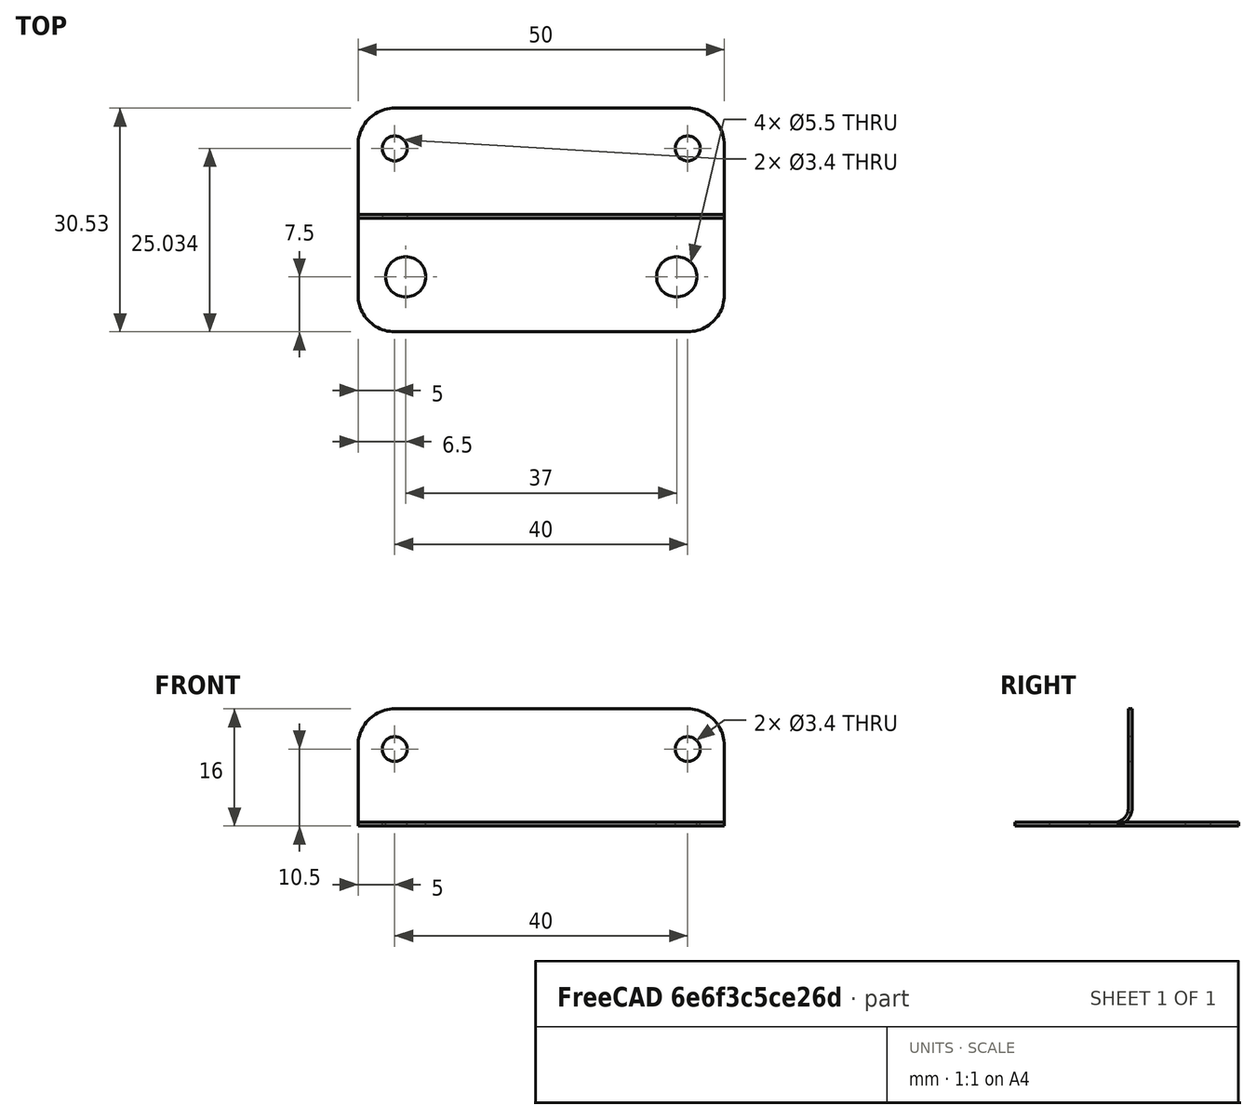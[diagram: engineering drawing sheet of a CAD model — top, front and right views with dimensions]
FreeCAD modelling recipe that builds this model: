
FCSTD DOCUMENT  (FreeCAD 1.1R38827 (Git))
Label: ugol90degX40mm
License: All rights reserved
LicenseURL: http://en.wikipedia.org/wiki/All_rights_reserved
objects: TechDraw::DrawViewDimension×10, Sketcher::SketchObject×8, PartDesign::SubShapeBinder×3, TechDraw::DrawViewPart×3, PartDesign::Hole×2, PartDesign::FeaturePython×1, TechDraw::DrawSVGTemplate×1, PartDesign::CoordinateSystem×1, PartDesign::Fillet×1, PartDesign::Mirrored×1, PartDesign::Body×1, Part::Feature×1, TechDraw::DrawPage×1
note: 38 computed .brp shape members not serialized (recipe doc carries the construction recipe); baked Part::Feature solids carry a one-line shape summary decoded from their .brp

FEATURE [Sketcher::SketchObject] Sketch
  ArcFitTolerance = 0
  AttachmentSupport = -> [YZ_Plane]
  FullyConstrained = true
  MakeInternals = false
  MapMode = 5
  Placement = pos=(0,0,0) rot=(0.57735,0.57735,0.57735;2.0944rad)
  sketch-geometry (2):
    g0: LineSegment StartX=-16 StartY=0 StartZ=0 EndX=0 EndY=0 EndZ=0
    g1: LineSegment StartX=0 StartY=0 StartZ=0 EndX=0 EndY=16 EndZ=0
  constraints (6):
    c: PointOnObject(g0,g-1)
    c: Coincident(g0,g-1)
    c: Coincident(g0,g1)
    c: PointOnObject(g1,g-2)
    c: DistanceX(g0,g0) = 16  'length'
    c: DistanceY(g1,g1) = 16  'height'
FEATURE [PartDesign::FeaturePython] BaseBend  # WARN: FeaturePython — macro-defined, semantics opaque (R4)
  BendSide = 1
  BendSketch = -> Sketch
  MidPlane = true
  Reverse = false
  Suppressed = false
  length = 50
  radius = 2
  thickness = 0.5
FEATURE [Sketcher::SketchObject] Sketch001
  ArcFitTolerance = 0
  AttachmentOffset = pos=(0,-8.5,0) rot=(0,0,1;0rad)
  AttachmentSupport = -> [XY_Plane]
  FullyConstrained = true
  MakeInternals = false
  MapMode = 5
  Placement = pos=(0,-8.5,0) rot=(0,0,1;0rad)
  sketch-geometry (2):
    g0: Circle CenterX=18.5 CenterY=0 CenterZ=0 NormalX=0 NormalY=0 NormalZ=1 AngleXU=0 Radius=1.7
    g1: Circle CenterX=-18.5 CenterY=0 CenterZ=0 NormalX=0 NormalY=0 NormalZ=1 AngleXU=0 Radius=1.7
  constraints (5):
    c: PointOnObject(g0,g-1)
    c: Equal(g1,g0)
    c: Diameter(g1) = 3.4
    c: Symmetric(g0,g1,g-2)
    c: DistanceX(g1,g0) = 37
FEATURE [PartDesign::SubShapeBinder] Binder  label="hor"
  BindCopyOnChange = 0
  BindMode = 0
  ClaimChildren = true
  Context = -> Body [Binder.]
  Fuse = false
  MakeFace = true
  OffsetFill = false
  OffsetIntersection = false
  OffsetJoinType = 0
  OffsetOpenResult = false
  PartialLoad = false
  Relative = true
  Support = -> [Sketch001]
  _Version = 2
FEATURE [PartDesign::SubShapeBinder] Binder001
  BindCopyOnChange = 0
  BindMode = 0
  ClaimChildren = false
  Context = -> Body [Binder001.]
  Fuse = false
  MakeFace = true
  OffsetFill = false
  OffsetIntersection = false
  OffsetJoinType = 0
  OffsetOpenResult = false
  PartialLoad = false
  Placement = pos=(0,0,0) rot=(-1,0,0;1.5708rad)
  Relative = true
  Support = -> [Sketch001]
  _Version = 2
FEATURE [PartDesign::SubShapeBinder] Binder002  label="vert"
  BindCopyOnChange = 0
  BindMode = 0
  ClaimChildren = true
  Context = -> Body [Binder002.]
  Fuse = false
  MakeFace = true
  OffsetFill = false
  OffsetIntersection = false
  OffsetJoinType = 0
  OffsetOpenResult = false
  PartialLoad = false
  Relative = true
  Support = -> [Sketch003]
  _Version = 2
  expr: Support = Sketch003._self
FEATURE [PartDesign::Hole] Hole
  BaseFeature = -> BaseBend
  CustomThreadClearance = 0
  Depth = 25
  DepthType = 0
  Diameter = 5.5
  DrillForDepth = false
  DrillPoint = 1
  DrillPointAngle = 118
  HoleCutCountersinkAngle = 90
  HoleCutCustomValues = false
  HoleCutDepth = 0
  HoleCutDiameter = 6.1
  HoleCutType = 0
  ModelThread = false
  Profile = -> Binder
  Reversed = true
  Suppressed = false
  Tapered = false
  TaperedAngle = 90
  ThreadClass = 0
  ThreadDepth = 25
  ThreadDepthType = 0
  ThreadDirection = 0
  ThreadFit = 0
  ThreadSize = 0
  ThreadType = 0
  Threaded = false
  UseCustomThreadClearance = false
FEATURE [PartDesign::Hole] Hole001
  BaseFeature = -> Hole
  CustomThreadClearance = 0
  Depth = 25
  DepthType = 0
  Diameter = 3.4
  DrillForDepth = false
  DrillPoint = 1
  DrillPointAngle = 118
  HoleCutCountersinkAngle = 90
  HoleCutCustomValues = false
  HoleCutDepth = 0
  HoleCutDiameter = 6.1
  HoleCutType = 0
  ModelThread = false
  Profile = -> Binder002
  Suppressed = false
  Tapered = false
  TaperedAngle = 90
  ThreadClass = 0
  ThreadDepth = 25
  ThreadDepthType = 0
  ThreadDirection = 0
  ThreadFit = 0
  ThreadSize = 0
  ThreadType = 0
  Threaded = false
  UseCustomThreadClearance = false
FEATURE [Sketcher::SketchObject] Sketch002
  ArcFitTolerance = 0
  AttachmentOffset = pos=(25,-16,0) rot=(0,0,1;-1.5708rad)
  AttachmentSupport = -> [XY_Plane]
  FullyConstrained = true
  MakeInternals = false
  MapMode = 5
  Placement = pos=(25,-16,0) rot=(0,0,1;4.71239rad)
  expr: .AttachmentOffset.Base.x = BaseBend.length / 2
  expr: .AttachmentOffset.Base.y = -Sketch.Constraints.length
  sketch-geometry (3):
    g0: ArcOfCircle CenterX=-5 CenterY=-5 CenterZ=0 NormalX=0 NormalY=0 NormalZ=1 AngleXU=0 Radius=5 StartAngle=0 EndAngle=1.5708
    g1: LineSegment StartX=-1.6e-14 StartY=-5 StartZ=0 EndX=-1.6e-14 EndY=-1.6e-14 EndZ=0
    g2: LineSegment StartX=-1.6e-14 StartY=-1.6e-14 StartZ=0 EndX=-5 EndY=-1.6e-14 EndZ=0
  constraints (8):
    c: PointOnObject(g0,g-1)
    c: PointOnObject(g0,g-2)
    c: Coincident(g1,g2)
    c: Horizontal(g2)
    c: Vertical(g1)
    c: Tangent(g0,g1) = -1.5708
    c: Tangent(g2,g0) = -1.5708
    c: Diameter(g0) = 10
FEATURE [TechDraw::DrawSVGTemplate] Template
  Height = 210
  Orientation = 1
  Template = <path>
  Width = 297
FEATURE [PartDesign::CoordinateSystem] Local_CS
  AttacherType = Attacher::AttachEngine3D
  AttachmentSupport = -> [XY_Plane]
  MapMode = 5
FEATURE [Sketcher::SketchObject] Sketch003
  ArcFitTolerance = 0
  AttachmentSupport = -> [XZ_Plane]
  FullyConstrained = true
  MakeInternals = false
  MapMode = 5
  Placement = pos=(0,0,0) rot=(1,0,0;1.5708rad)
  expr: Constraints[3] = 3.4
  sketch-geometry (2):
    g0: Circle CenterX=20 CenterY=10.5 CenterZ=0 NormalX=0 NormalY=0 NormalZ=1 AngleXU=0 Radius=1.7
    g1: Circle CenterX=-20 CenterY=10.5 CenterZ=0 NormalX=0 NormalY=0 NormalZ=1 AngleXU=0 Radius=1.7
  constraints (5):
    c: Symmetric(g1,g0,g-2)
    c: DistanceX(g1,g0) = 40
    c: Equal(g0,g1)
    c: Diameter(g0) = 3.4
    c: DistanceY(g0) = 10.5
FEATURE [PartDesign::Fillet] Fillet
  Base = -> Hole001 [Edge33,Edge15]
  BaseFeature = -> Hole001
  Radius = 5
  SupportTransform = false
  Suppressed = false
  UseAllEdges = false
FEATURE [PartDesign::Mirrored] Mirrored
  BaseFeature = -> Fillet
  MirrorPlane = -> YZ_Plane
  Originals = -> [Fillet]
  Suppressed = false
  TransformMode = 0
FEATURE [PartDesign::Body] Body  label="Body_material_0.50ansi"
  AllowCompound = false
  Group = -> [Sketch,BaseBend,Sketch001,Binder,Binder001,Binder002,Hole,Hole001,Sketch002,Local_CS,Sketch003,Fillet,Mirrored]
  Origin = -> Origin
  Tip = -> Mirrored
FEATURE [TechDraw::DrawViewPart] View
  CoarseView = false
  Direction = (1,0,0)
  Focus = 100
  HardHidden = false
  IsoCount = 0
  IsoHidden = false
  IsoVisible = false
  LockPosition = false
  Perspective = false
  Rotation = 0
  ScaleType = 0
  ScrubCount = 0
  SeamHidden = false
  SeamVisible = true
  SmoothHidden = false
  SmoothVisible = true
  Source = -> [Body]
  X = 234.919
  XDirection = (0,1,-1.19209e-07)
  Y = 105
  expr: Y = Template.Height / 2
FEATURE [TechDraw::DrawViewPart] View001
  CoarseView = false
  Direction = (0,-1,0)
  Focus = 100
  HardHidden = false
  IsoCount = 0
  IsoHidden = false
  IsoVisible = false
  LockPosition = false
  Perspective = false
  Rotation = 0
  ScaleType = 0
  ScrubCount = 0
  SeamHidden = false
  SeamVisible = true
  SmoothHidden = false
  SmoothVisible = true
  Source = -> [Body]
  X = 150.495
  XDirection = (1,0,0)
  Y = 105
  expr: Y = Template.Height / 2
FEATURE [TechDraw::DrawViewDimension] Dimension004
  AngleOverride = false
  Arbitrary = false
  ArbitraryTolerances = false
  EqualTolerance = true
  ExtensionAngle = 0
  FormatSpec = %.2w
  FormatSpecOverTolerance = %+.2w
  FormatSpecUnderTolerance = %+.2w
  Inverted = false
  LineAngle = 0
  LockPosition = false
  MeasureType = 1
  OverTolerance = 0
  References2D = -> [View001]
  Rotation = 0
  ScaleType = 0
  TheoreticalExact = false
  Type = 1
  UnderTolerance = 0
  X = -2.33735
  Y = 6.64929
FEATURE [TechDraw::DrawViewDimension] Dimension005
  AngleOverride = false
  Arbitrary = false
  ArbitraryTolerances = false
  EqualTolerance = true
  ExtensionAngle = 0
  FormatSpec = %.2w
  FormatSpecOverTolerance = %+.2w
  FormatSpecUnderTolerance = %+.2w
  Inverted = false
  LineAngle = 0
  LockPosition = false
  MeasureType = 1
  OverTolerance = 0
  References2D = -> [View]
  Rotation = 0
  ScaleType = 0
  TheoreticalExact = false
  Type = 1
  UnderTolerance = 0
  X = -0.501878
  Y = -11.8128
FEATURE [TechDraw::DrawViewDimension] Dimension006
  AngleOverride = false
  Arbitrary = false
  ArbitraryTolerances = false
  EqualTolerance = true
  ExtensionAngle = 0
  FormatSpec = %.2w
  FormatSpecOverTolerance = %+.2w
  FormatSpecUnderTolerance = %+.2w
  Inverted = false
  LineAngle = 0
  LockPosition = false
  MeasureType = 1
  OverTolerance = 0
  References2D = -> [View]
  Rotation = 0
  ScaleType = 0
  TheoreticalExact = false
  Type = 2
  UnderTolerance = 0
  X = 19.7679
  Y = 4.25841
FEATURE [TechDraw::DrawViewDimension] Dimension007
  AngleOverride = false
  Arbitrary = false
  ArbitraryTolerances = false
  EqualTolerance = true
  ExtensionAngle = 0
  FormatSpec = %.2w
  FormatSpecOverTolerance = %+.2w
  FormatSpecUnderTolerance = %+.2w
  Inverted = false
  LineAngle = 0
  LockPosition = false
  MeasureType = 1
  OverTolerance = 0
  References2D = -> [View001]
  Rotation = 0
  ScaleType = 0
  TheoreticalExact = false
  Type = 2
  UnderTolerance = 0
  X = -38.2507
  Y = 2.12999
FEATURE [TechDraw::DrawViewPart] View002
  CoarseView = false
  Direction = (0,0,1)
  Focus = 100
  HardHidden = false
  IsoCount = 0
  IsoHidden = false
  IsoVisible = false
  LockPosition = false
  Perspective = false
  Rotation = 0
  ScaleType = 0
  ScrubCount = 0
  SeamHidden = false
  SeamVisible = true
  SmoothHidden = false
  SmoothVisible = true
  Source = -> [Body]
  X = 59.88
  XDirection = (1,0,0)
  Y = 105
  expr: Y = Template.Height / 2
FEATURE [TechDraw::DrawViewDimension] Dimension008
  AngleOverride = false
  Arbitrary = false
  ArbitraryTolerances = false
  EqualTolerance = true
  ExtensionAngle = 0
  FormatSpec = %.2w
  FormatSpecOverTolerance = %+.2w
  FormatSpecUnderTolerance = %+.2w
  Inverted = false
  LineAngle = 0
  LockPosition = false
  MeasureType = 1
  OverTolerance = 0
  References2D = -> [View002]
  Rotation = 0
  ScaleType = 0
  TheoreticalExact = false
  Type = 2
  UnderTolerance = 0
  X = 32.5666
  Y = 27.4342
FEATURE [TechDraw::DrawViewDimension] Dimension009
  AngleOverride = false
  Arbitrary = false
  ArbitraryTolerances = false
  EqualTolerance = true
  ExtensionAngle = 0
  FormatSpec = %.2w
  FormatSpecOverTolerance = %+.2w
  FormatSpecUnderTolerance = %+.2w
  Inverted = false
  LineAngle = 0
  LockPosition = false
  MeasureType = 1
  OverTolerance = 0
  References2D = -> [View002]
  Rotation = 0
  ScaleType = 0
  TheoreticalExact = false
  Type = 1
  UnderTolerance = 0
  X = 3.55389
  Y = -20.9787
FEATURE [TechDraw::DrawViewDimension] Dimension010
  AngleOverride = false
  Arbitrary = false
  ArbitraryTolerances = false
  EqualTolerance = true
  ExtensionAngle = 0
  FormatSpec = ⌀%.2w
  FormatSpecOverTolerance = %+.2w
  FormatSpecUnderTolerance = %+.2w
  Inverted = false
  LineAngle = 0
  LockPosition = false
  MeasureType = 1
  OverTolerance = 0
  References2D = -> [View002]
  Rotation = 0
  ScaleType = 0
  TheoreticalExact = false
  Type = 5
  UnderTolerance = 0
  X = 0
  Y = 0
FEATURE [TechDraw::DrawViewDimension] Dimension011
  AngleOverride = false
  Arbitrary = false
  ArbitraryTolerances = false
  EqualTolerance = true
  ExtensionAngle = 0
  FormatSpec = ⌀%.2w
  FormatSpecOverTolerance = %+.2w
  FormatSpecUnderTolerance = %+.2w
  Inverted = false
  LineAngle = 0
  LockPosition = false
  MeasureType = 1
  OverTolerance = 0
  References2D = -> [View001]
  Rotation = 0
  ScaleType = 0
  TheoreticalExact = false
  Type = 5
  UnderTolerance = 0
  X = 4.12404
  Y = 22.7037
FEATURE [TechDraw::DrawViewDimension] Dimension
  AngleOverride = false
  Arbitrary = false
  ArbitraryTolerances = false
  BoxCorners = (2) [(-25,-8,-1e-07),(25,8,1e-07)]
  EqualTolerance = true
  ExtensionAngle = 0
  FormatSpec = %.2w
  FormatSpecOverTolerance = %+.2w
  FormatSpecUnderTolerance = %+.2w
  Inverted = false
  LineAngle = 0
  LockPosition = false
  MeasureType = 1
  OverTolerance = 0
  References2D = -> [View001]
  Rotation = 0
  ScaleType = 0
  TheoreticalExact = false
  Type = 1
  UnderTolerance = 0
  X = 0.093135
  Y = -9.9705
FEATURE [Part::Feature] Unfold
  shape: bbox 50 x 30.53 x 0.5612 mm, 14 faces (baked)
FEATURE [Sketcher::SketchObject] Unfold_Sketch
  ArcFitTolerance = 0
  FullyConstrained = false
  MakeInternals = false
  sketch-geometry (12):
    g0: BSplineCurve PolesCount=22 KnotsCount=5 Degree=6 IsPeriodic=0
    g1: LineSegment StartX=-20 StartY=14.5343 StartZ=0 EndX=20 EndY=14.5343 EndZ=0
    g2: BSplineCurve PolesCount=22 KnotsCount=5 Degree=6 IsPeriodic=0
    g3: LineSegment StartX=-25 StartY=-11 StartZ=0 EndX=-25 EndY=9.53429 EndZ=0
    g4: BSplineCurve PolesCount=22 KnotsCount=5 Degree=6 IsPeriodic=0
    g5: LineSegment StartX=-20 StartY=-16 StartZ=0 EndX=20 EndY=-16 EndZ=0
    g6: BSplineCurve PolesCount=22 KnotsCount=5 Degree=6 IsPeriodic=0
    g7: LineSegment StartX=25 StartY=-11 StartZ=0 EndX=25 EndY=9.53429 EndZ=0
    g8: Circle CenterX=18.5 CenterY=-8.5 CenterZ=0 NormalX=0 NormalY=0 NormalZ=1 AngleXU=-3.14159 Radius=2.75
    g9: Circle CenterX=-18.5 CenterY=-8.5 CenterZ=0 NormalX=0 NormalY=0 NormalZ=1 AngleXU=-3.14159 Radius=2.75
    g10: Circle CenterX=20 CenterY=9.03429 CenterZ=0 NormalX=0 NormalY=0 NormalZ=1 AngleXU=-5e-16 Radius=1.7
    g11: Circle CenterX=-20 CenterY=9.03429 CenterZ=0 NormalX=0 NormalY=0 NormalZ=1 AngleXU=-5e-16 Radius=1.7
FEATURE [Sketcher::SketchObject] Unfold_Sketch_Outline
  ArcFitTolerance = 0
  FullyConstrained = false
  MakeInternals = false
  sketch-geometry (8):
    g0: BSplineCurve PolesCount=22 KnotsCount=5 Degree=6 IsPeriodic=0
    g1: LineSegment StartX=-20 StartY=14.5343 StartZ=0 EndX=20 EndY=14.5343 EndZ=0
    g2: BSplineCurve PolesCount=22 KnotsCount=5 Degree=6 IsPeriodic=0
    g3: LineSegment StartX=25 StartY=-11 StartZ=0 EndX=25 EndY=9.53429 EndZ=0
    g4: BSplineCurve PolesCount=22 KnotsCount=5 Degree=6 IsPeriodic=0
    g5: LineSegment StartX=-20 StartY=-16 StartZ=0 EndX=20 EndY=-16 EndZ=0
    g6: BSplineCurve PolesCount=22 KnotsCount=5 Degree=6 IsPeriodic=0
    g7: LineSegment StartX=-25 StartY=-11 StartZ=0 EndX=-25 EndY=9.53429 EndZ=0
FEATURE [Sketcher::SketchObject] Unfold_Sketch_Internal
  ArcFitTolerance = 0
  FullyConstrained = false
  MakeInternals = false
  sketch-geometry (4):
    g0: Circle CenterX=-18.5 CenterY=-8.5 CenterZ=0 NormalX=0 NormalY=0 NormalZ=1 AngleXU=-3.14159 Radius=2.75
    g1: Circle CenterX=18.5 CenterY=-8.5 CenterZ=0 NormalX=0 NormalY=0 NormalZ=1 AngleXU=-3.14159 Radius=2.75
    g2: Circle CenterX=-20 CenterY=9.03429 CenterZ=0 NormalX=0 NormalY=0 NormalZ=1 AngleXU=-5e-16 Radius=1.7
    g3: Circle CenterX=20 CenterY=9.03429 CenterZ=0 NormalX=0 NormalY=0 NormalZ=1 AngleXU=-5e-16 Radius=1.7
FEATURE [Sketcher::SketchObject] Unfold_Sketch_bends
  ArcFitTolerance = 0
  FullyConstrained = false
  MakeInternals = false
  Placement = pos=(0,-0.322113,0.363738) rot=(1,0,0;0.724782rad)
  sketch-geometry (1):
    g0: LineSegment StartX=25 StartY=-0.548647 StartZ=0 EndX=-25 EndY=-0.548647 EndZ=0
FEATURE [TechDraw::DrawViewDimension] Dimension012
  AngleOverride = false
  Arbitrary = false
  ArbitraryTolerances = false
  EqualTolerance = true
  ExtensionAngle = 0
  FormatSpec = R%.2w
  FormatSpecOverTolerance = %+.2w
  FormatSpecUnderTolerance = %+.2w
  Inverted = false
  LineAngle = 0
  LockPosition = false
  MeasureType = 1
  OverTolerance = 0
  References2D = -> [View]
  Rotation = 0
  ScaleType = 0
  TheoreticalExact = false
  Type = 4
  UnderTolerance = 0
  X = 1.47523
  Y = 5.22752
FEATURE [TechDraw::DrawPage] Page
  KeepUpdated = true
  NextBalloonIndex = 1
  ProjectionType = 0
  Template = -> Template
  Views = -> [View,View001,Dimension004,Dimension005,Dimension006,Dimension007,View002,Dimension008,Dimension009,Dimension010,Dimension011,Dimension,Dimension012]
note: 1 file-system path scrubbed to <path> (originals preserved in the JSON sidecar)
